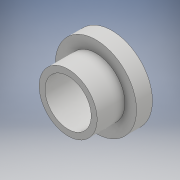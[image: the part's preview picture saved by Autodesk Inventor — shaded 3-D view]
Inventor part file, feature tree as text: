
AUTODESK INVENTOR PART (.ipt)
format: ipt  version: 2019 (Build 230136000, 136)  size: 253,440 bytes
history: native  units: mm
features: sketch x2, revolve x1, extrude x1
ambient origin geometry x8: Origin, YZ Plane, XZ Plane, XY Plane, X Axis, Y Axis, Z Axis, Center Point
bodies: Solid1 (feature_tree)
feature tree (4):
  revolve  "Revolution1"  [1 undecoded]
  extrude  "Extrusion1"  Depth=6.0mm
  sketch  "Sketch2"  dims[d4=8.4mm d5=3.3mm]
  sketch  "Sketch4"  dims[d6=5.75mm d8=6.0mm d10=90.0deg d11=0.5mm d12=0.0mm]
note: 1 required parameter value undecoded (feature->parameter linkage not recoverable at this tier; creation-order binding heuristic only, values carry confidence <= 0.55)
